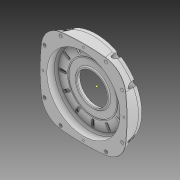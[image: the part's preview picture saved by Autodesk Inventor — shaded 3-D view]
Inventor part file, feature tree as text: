
AUTODESK INVENTOR PART (.ipt)
format: ipt  version: 2020 (Build 240168000, 168)  size: 950,272 bytes
history: native  units: mm
features: sketch x21, extrude x17, projected_geometry x5, other x4, plane x3, fillet x2, loft x1, revolve x1, pattern_circular x1, chamfer x1
ambient origin geometry x8: Origin, YZ Plane, XZ Plane, XY Plane, X Axis, Y Axis, Z Axis, Center Point
bodies: Solid1 (feature_tree)
feature tree (56):
  other  "Blocks"
  sketch  "Sketch1"  dims[d1=170.0mm d2=170.0mm]
  extrude  "Extrusion1"  Depth=170.0mm
  extrude  "Extrusion2"  Depth=60.0mm TaperAngle=0.0deg
  plane  "Work Plane1"
  loft  "Loft1"
  extrude  "Extrusion3"  Depth=7.5mm
  plane  "Work Plane2"
  sketch  "Sketch6"  dims[d14=17.5mm d15=7.5mm]
  plane  "Work Plane3"
  sketch  "Sketch7"  dims[d16=10.0mm d17=65.0mm]
  extrude  "Extrusion4"  Depth=7.5mm
  extrude  "Extrusion5"  Depth=7.5mm
  extrude  "Extrusion9"  Depth=10.0mm
  sketch  "Sketch13"  dims[d23=0.0mm d24=90.0deg d25=5.0mm d26=0.0mm]
  extrude  "Extrusion10"  Depth=7.5mm
  extrude  "Extrusion11"  TaperAngle=0.0deg  [1 undecoded]
  extrude  "Extrusion12"  Depth=5.0mm TaperAngle=0.0deg
  revolve  "Revolution1"  [1 undecoded]
  extrude  "Extrusion13"  Depth=4.0mm
  extrude  "Extrusion14"  Depth=10.0mm
  extrude  "Extrusion15"  Depth=6.0mm TaperAngle=0.0deg
  fillet  "Fillet1"  Radius=6.0mm
  extrude  "Extrusion16"  Depth=47.0mm
  fillet  "Fillet3"  Radius=60.0mm
  pattern_circular  "Circular Pattern1"  Count=6  [1 undecoded]
  extrude  "Extrusion17"  Depth=42.0mm
  extrude  "Extrusion18"  Depth=40.0mm
  extrude  "Extrusion19"  Depth=6.0mm
  extrude  "Extrusion20"  Depth=6.0mm TaperAngle=0.0deg
  chamfer  "Chamfer1"  Angle=90.0deg  [1 undecoded]
  sketch  "Sketch24"  dims[d78=7.0mm d81=90.0deg d82=59.39697mm d83=10.0mm d85=6.2mm d86=9.0mm d87=40.0mm d89=360.0deg d91=48.25mm d92=0.0mm d93=9.0mm d94=40.0mm d96=360.0deg d98=20.0mm d99=0.0mm d100=0.0mm d101=0.0mm d104=45.0deg d105=32.6mm d107=2.0mm d108=7.0mm d109=35.0mm d110=2.0mm d111=135.0deg d112=8.0mm d113=4.0mm d115=60.0mm d116=2.5mm d117=10.0mm d118=10.0mm d119=0.0mm d120=120.0mm d121=360.0deg d123=4.0mm d124=80.0mm d125=3.3mm d126=40.0mm d128=360.0deg d130=0.0mm d131=0.0mm d133=5.7mm d134=40.0mm d136=360.0deg d138=6.0mm d139=0.0mm d140=95.5mm d141=2.0mm d142=0.8mm d143=0.0mm d144=95.5mm d145=69.5mm d146=0.8mm d147=0.0mm d148=32.0mm d149=0.5mm d150=2.0mm d151=45.0deg]
  sketch  "Sketch2"  dims[d3=40.0mm d4=60.0mm d5=0.0mm]
  other  "Block1"
  sketch  "Sketch3"  dims[d7=0.0mm d8=0.0mm d9=5.5mm]
  sketch  "Sketch4"  dims[d10=57.5mm d11=7.5mm]
  projected_geometry  "Projected Loop1"
  sketch  "Sketch5"  dims[d12=7.5mm d13=7.5mm]
  projected_geometry  "Projected Loop2"
  projected_geometry  "Projected Loop3"
  projected_geometry  "Projected Loop4"
  sketch  "Sketch8"  dims[d18=7.5mm d19=7.5mm]
  sketch  "Sketch12"  dims[d20=25.0mm d21=0.0mm d22=90.0deg]
  projected_geometry  "Projected Loop5"
  sketch  "Sketch14"  dims[d27=180.0mm d28=-3.0mm]
  sketch  "Sketch15"  dims[d29=2.5mm d30=4.0mm]
  sketch  "Sketch16"  dims[d31=10.0mm d32=0.0mm d33=145.0mm]
  sketch  "Sketch17"  dims[d34=48.25mm d35=0.0mm d54=60.0mm d55=0.0mm d56=6.0mm d57=0.0mm]
  sketch  "Sketch18"  dims[d58=47.0mm d59=47.0mm d60=60.0mm d61=60.0mm]
  sketch  "Sketch19"  dims[d62=42.0mm d63=42.0mm]
  sketch  "Sketch20"  dims[d64=5.5mm d65=40.0mm]
  sketch  "Sketch21"  dims[d66=6.0mm d67=0.0mm d68=22.1mm]
  sketch  "Sketch22"  dims[d69=16.0mm d70=6.0mm d71=0.0mm]
  sketch  "Sketch23"  dims[d74=25.0mm]
  other  "Block1:1"
  other  "Block1:2"
note: 4 required parameter values undecoded (feature->parameter linkage not recoverable at this tier; creation-order binding heuristic only, values carry confidence <= 0.55)